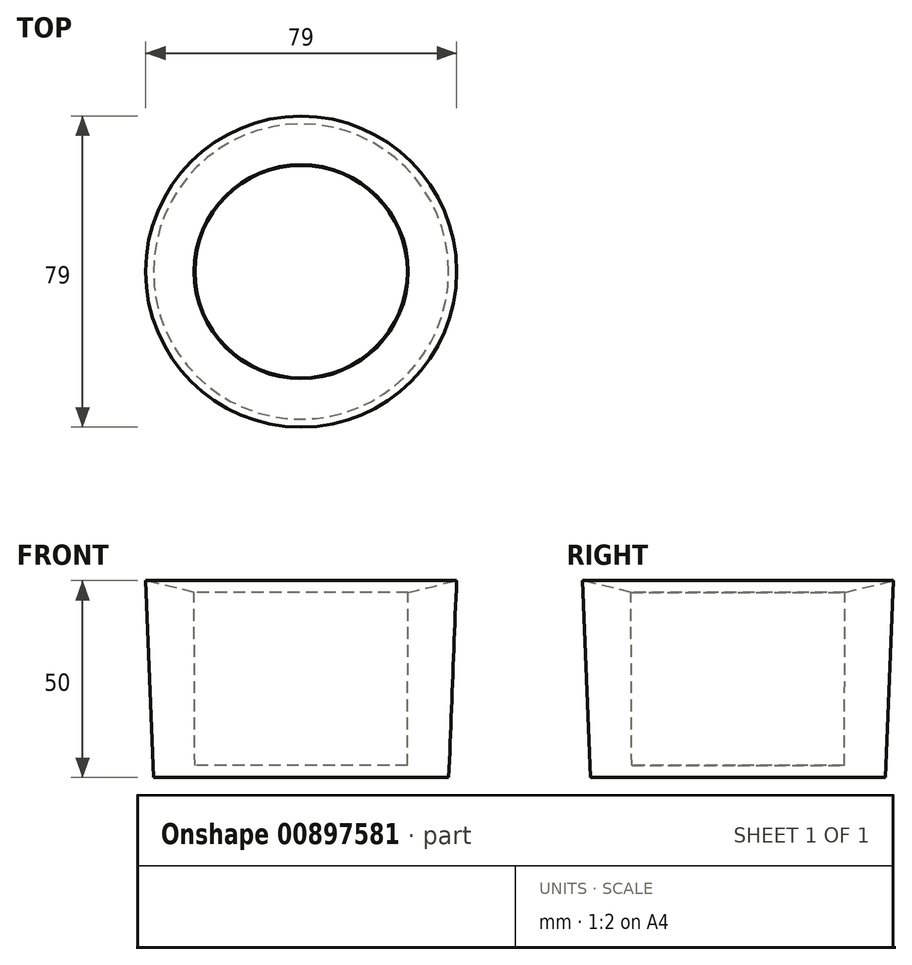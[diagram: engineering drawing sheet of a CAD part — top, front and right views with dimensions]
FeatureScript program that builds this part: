
annotation { "Feature Type Name" : "Feature", "Feature Type Description" : "" }
export const myFeature = defineFeature(function(context is Context, id is Id, definition is map)
    precondition{}
    {
        {
            var Q0;
            Q0=qCreatedBy(makeId("Front.planeOp"),FACE);
            var sketch = newSketch(context, id + "F0", { "sketchPlane" : qUnion([Q0])});
            skLineSegment(sketch, "E0", {"start": v(0, 0) * mm, "end": v(37.5, 0) * mm});
            skLineSegment(sketch, "E1", {"start": v(37.5, 0) * mm, "end": v(39.5, 50) * mm});
            skLineSegment(sketch, "E2", {"start": v(27, 3) * mm, "end": v(27.2, 47) * mm});
            skLineSegment(sketch, "E3", {"start": v(27.2, 47) * mm, "end": v(39.5, 50) * mm});
            skPoint(sketch, "E4", {"position": v(0, 0) * mm});
            skLineSegment(sketch, "E5", {"start": v(27, 3) * mm, "end": v(0, 3) * mm});
            skLineSegment(sketch, "E6", {"start": v(0, 3) * mm, "end": v(0, 0) * mm});
            skSolve(sketch);
        }
        {
            var Q0;
            Q0=makeQuery(id+"F0.imprint","IMPRINT",FACE,{"disambiguationData":[TD([[makeQuery(id+"F0.imprint","IMPRINT",EDGE,{"derivedFrom":sQuery(id+"F0.wireOp",EDGE,"E0")}),1.0]])]});
            var Q1;
            Q1=sQuery(id+"F0.wireOp",EDGE,"E6");
            revolve(context, id + "F1", {"surfaceOperationType" : NewSurfaceOperationType.NEW, "entities" : qUnion([Q0]), "axis" : qUnion([Q1]), "revolveType" : RevolveType.FULL});
        }
    });
